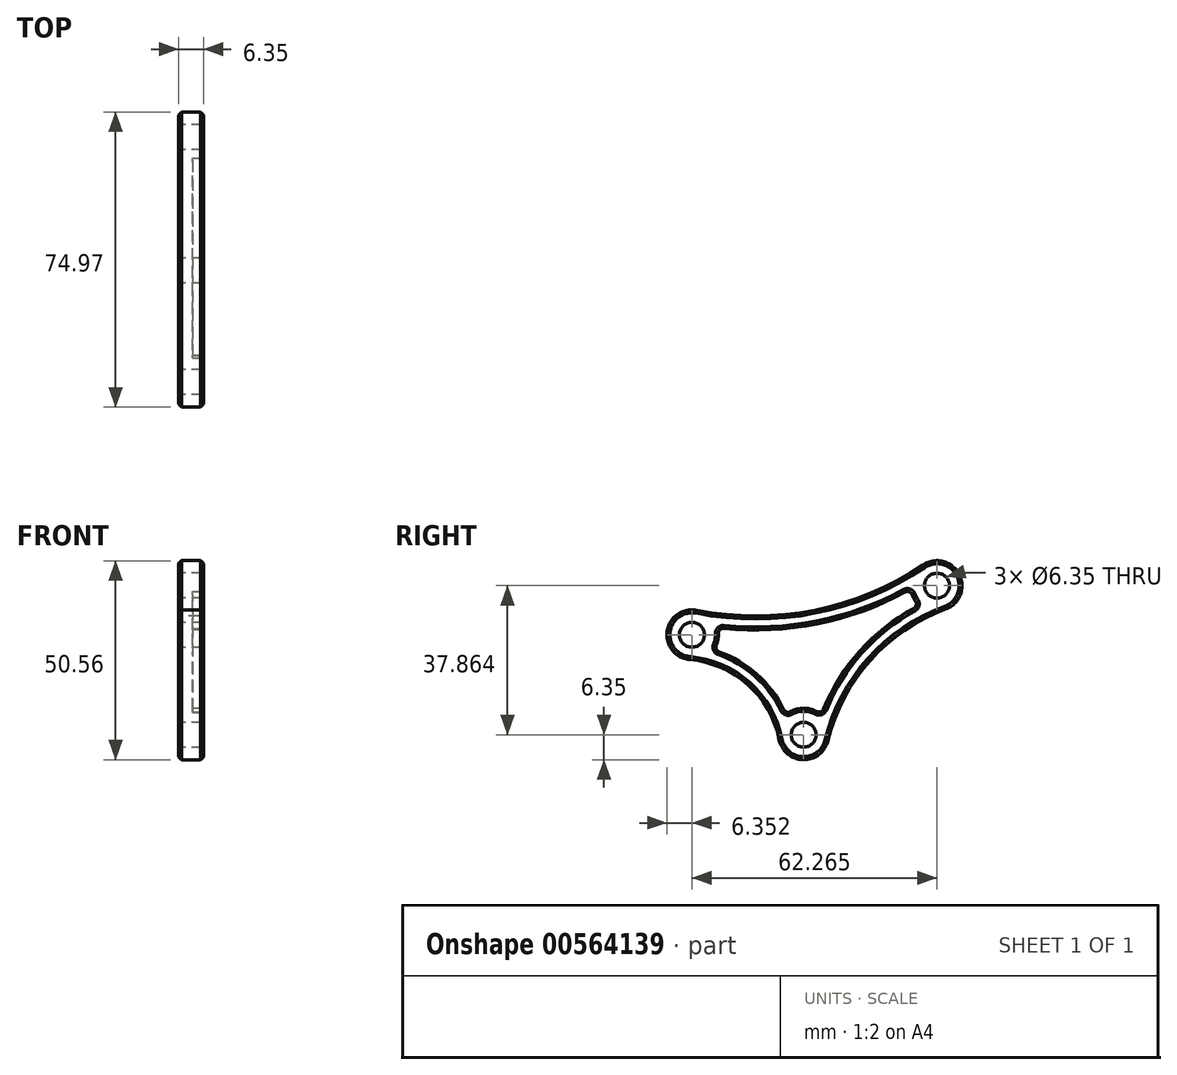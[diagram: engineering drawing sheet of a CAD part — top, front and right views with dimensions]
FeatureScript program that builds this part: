
annotation { "Feature Type Name" : "Feature", "Feature Type Description" : "" }
export const myFeature = defineFeature(function(context is Context, id is Id, definition is map)
    precondition{}
    {
        {
            var Q0;
            Q0=qCreatedBy(makeId("Right.planeOp"),FACE);
            var sketch = newSketch(context, id + "F0", { "sketchPlane" : qUnion([Q0])});
            skCircle(sketch, "E0", {"center": v(0, 0) * mm, "radius": 3.18 * mm});
            skCircle(sketch, "E1", {"center": v(33.87, 37.86) * mm, "radius": 3.18 * mm});
            skCircle(sketch, "E2", {"center": v(-28.4, 25.4) * mm, "radius": 3.18 * mm});
            skCircle(sketch, "E3", {"center": v(-28.4, 25.4) * mm, "radius": 6.35 * mm});
            skCircle(sketch, "E4", {"center": v(33.87, 37.86) * mm, "radius": 6.35 * mm});
            skCircle(sketch, "E5", {"center": v(0, 0) * mm, "radius": 6.35 * mm});
            skLineSegment(sketch, "E6", {"start": v(-28.4, 25.4) * mm, "end": v(33.87, 37.86) * mm});
            skLineSegment(sketch, "E7", {"start": v(0, 0) * mm, "end": v(-28.4, 25.4) * mm});
            skLineSegment(sketch, "E8", {"start": v(33.87, 37.86) * mm, "end": v(0, 0) * mm});
            skArc(sketch, "E9", {"start": v(-27.15, 31.63) * mm, "mid": v(2.73, 31.63) * mm, "end": v(30.32, 43.13) * mm});
            skArc(sketch, "E10", {"start": v(-6.23, -1.25) * mm, "mid": v(-14.2, 12.7) * mm, "end": v(-28.94, 19.07) * mm});
            skArc(sketch, "E11", {"start": v(36.05, 31.9) * mm, "mid": v(16.93, 18.93) * mm, "end": v(6.17, -1.5) * mm});
            skSolve(sketch);
        }
        {
            var Q0;
            {var subQ0=sQuery(id+"F0.wireOp",EDGE,"E9");var subQ1=sQuery(id+"F0.wireOp",EDGE,"E3");var subQ2=makeQuery(id+"F0.imprint","INTERSECT",VERTEX,{"derivedFrom":[subQ1,subQ0]});Q0=makeQuery(id+"F0.imprint","IMPRINT",FACE,{"disambiguationData":[TD([[makeQuery(id+"F0.imprint","IMPRINT",EDGE,{"disambiguationData":[TD([[subQ2,1.0]])],"derivedFrom":subQ1}),-1.0]])]});}
            var Q1;
            {var subQ0=sQuery(id+"F0.wireOp",EDGE,"E10");var subQ1=sQuery(id+"F0.wireOp",EDGE,"E3");var subQ2=makeQuery(id+"F0.imprint","INTERSECT",VERTEX,{"derivedFrom":[subQ1,subQ0]});Q1=makeQuery(id+"F0.imprint","IMPRINT",FACE,{"disambiguationData":[TD([[makeQuery(id+"F0.imprint","IMPRINT",EDGE,{"disambiguationData":[TD([[subQ2,-1.0]])],"derivedFrom":subQ1}),-1.0]])]});}
            var Q2;
            {var subQ0=sQuery(id+"F0.wireOp",EDGE,"E9");var subQ1=sQuery(id+"F0.wireOp",EDGE,"E4");var subQ2=makeQuery(id+"F0.imprint","INTERSECT",VERTEX,{"derivedFrom":[subQ1,subQ0]});Q2=makeQuery(id+"F0.imprint","IMPRINT",FACE,{"disambiguationData":[TD([[makeQuery(id+"F0.imprint","IMPRINT",EDGE,{"disambiguationData":[TD([[subQ2,-1.0]])],"derivedFrom":subQ1}),-1.0]])]});}
            var Q3;
            {var subQ0=sQuery(id+"F0.wireOp",EDGE,"E10");var subQ1=sQuery(id+"F0.wireOp",EDGE,"E5");var subQ2=makeQuery(id+"F0.imprint","INTERSECT",VERTEX,{"derivedFrom":[subQ1,subQ0]});Q3=makeQuery(id+"F0.imprint","IMPRINT",FACE,{"disambiguationData":[TD([[makeQuery(id+"F0.imprint","IMPRINT",EDGE,{"disambiguationData":[TD([[subQ2,1.0]])],"derivedFrom":subQ1}),-1.0]])]});}
            var Q4;
            {var subQ5=sQuery(id+"F0.wireOp",EDGE,"E7");var subQ6=sQuery(id+"F0.wireOp",EDGE,"E0");var subQ7=makeQuery(id+"F0.imprint","INTERSECT",VERTEX,{"derivedFrom":[subQ6,subQ5]});Q4=makeQuery(id+"F0.imprint","IMPRINT",FACE,{"disambiguationData":[TD([[makeQuery(id+"F0.imprint","IMPRINT",EDGE,{"disambiguationData":[TD([[subQ7,-1.0]])],"derivedFrom":subQ6}),-1.0]])]});}
            var Q5;
            {var subQ5=sQuery(id+"F0.wireOp",EDGE,"E6");var subQ7=sQuery(id+"F0.wireOp",EDGE,"E1");var subQ8=makeQuery(id+"F0.imprint","INTERSECT",VERTEX,{"derivedFrom":[subQ7,subQ5]});Q5=makeQuery(id+"F0.imprint","IMPRINT",FACE,{"disambiguationData":[TD([[makeQuery(id+"F0.imprint","IMPRINT",EDGE,{"disambiguationData":[TD([[subQ8,1.0]])],"derivedFrom":subQ7}),-1.0]])]});}
            var Q6;
            {var subQ4=sQuery(id+"F0.wireOp",EDGE,"E6");var subQ5=sQuery(id+"F0.wireOp",EDGE,"E2");var subQ6=makeQuery(id+"F0.imprint","INTERSECT",VERTEX,{"derivedFrom":[subQ5,subQ4]});Q6=makeQuery(id+"F0.imprint","IMPRINT",FACE,{"disambiguationData":[TD([[makeQuery(id+"F0.imprint","IMPRINT",EDGE,{"disambiguationData":[TD([[subQ6,-1.0]])],"derivedFrom":subQ5}),-1.0]])]});}
            var Q7;
            {var subQ0=sQuery(id+"F0.wireOp",EDGE,"E6");var subQ2=sQuery(id+"F0.wireOp",EDGE,"E3");var subQ3=makeQuery(id+"F0.imprint","INTERSECT",VERTEX,{"derivedFrom":[subQ2,subQ0]});Q7=makeQuery(id+"F0.imprint","IMPRINT",FACE,{"disambiguationData":[TD([[makeQuery(id+"F0.imprint","IMPRINT",EDGE,{"disambiguationData":[TD([[subQ3,1.0]])],"derivedFrom":subQ2}),-1.0]])]});}
            var Q8;
            {var subQ0=sQuery(id+"F0.wireOp",EDGE,"E6");var subQ1=sQuery(id+"F0.wireOp",EDGE,"E2");var subQ2=makeQuery(id+"F0.imprint","INTERSECT",VERTEX,{"derivedFrom":[subQ1,subQ0]});Q8=makeQuery(id+"F0.imprint","IMPRINT",FACE,{"disambiguationData":[TD([[makeQuery(id+"F0.imprint","IMPRINT",EDGE,{"disambiguationData":[TD([[subQ2,1.0]])],"derivedFrom":subQ1}),-1.0]])]});}
            var Q9;
            {var subQ0=sQuery(id+"F0.wireOp",EDGE,"E6");var subQ1=sQuery(id+"F0.wireOp",EDGE,"E1");var subQ2=makeQuery(id+"F0.imprint","INTERSECT",VERTEX,{"derivedFrom":[subQ1,subQ0]});Q9=makeQuery(id+"F0.imprint","IMPRINT",FACE,{"disambiguationData":[TD([[makeQuery(id+"F0.imprint","IMPRINT",EDGE,{"disambiguationData":[TD([[subQ2,-1.0]])],"derivedFrom":subQ1}),-1.0]])]});}
            var Q10;
            {var subQ0=sQuery(id+"F0.wireOp",EDGE,"E7");var subQ1=sQuery(id+"F0.wireOp",EDGE,"E0");var subQ2=makeQuery(id+"F0.imprint","INTERSECT",VERTEX,{"derivedFrom":[subQ1,subQ0]});Q10=makeQuery(id+"F0.imprint","IMPRINT",FACE,{"disambiguationData":[TD([[makeQuery(id+"F0.imprint","IMPRINT",EDGE,{"disambiguationData":[TD([[subQ2,1.0]])],"derivedFrom":subQ1}),-1.0]])]});}
            var Q11;
            {var subQ0=sQuery(id+"F0.wireOp",EDGE,"E11");var subQ1=sQuery(id+"F0.wireOp",EDGE,"E5");var subQ2=makeQuery(id+"F0.imprint","INTERSECT",VERTEX,{"derivedFrom":[subQ1,subQ0]});Q11=makeQuery(id+"F0.imprint","IMPRINT",FACE,{"disambiguationData":[TD([[makeQuery(id+"F0.imprint","IMPRINT",EDGE,{"disambiguationData":[TD([[subQ2,-1.0]])],"derivedFrom":subQ1}),-1.0]])]});}
            var Q12;
            {var subQ0=sQuery(id+"F0.wireOp",EDGE,"E11");var subQ1=sQuery(id+"F0.wireOp",EDGE,"E4");var subQ2=makeQuery(id+"F0.imprint","INTERSECT",VERTEX,{"derivedFrom":[subQ1,subQ0]});Q12=makeQuery(id+"F0.imprint","IMPRINT",FACE,{"disambiguationData":[TD([[makeQuery(id+"F0.imprint","IMPRINT",EDGE,{"disambiguationData":[TD([[subQ2,1.0]])],"derivedFrom":subQ1}),-1.0]])]});}
            var Q13;
            {var subQ7=sQuery(id+"F0.wireOp",EDGE,"s0z4VmjC-9Jtz-9oDN-pM9U-WHnKUmS6Y34w");Q13=makeQuery(id+"F0.imprint","IMPRINT",FACE,{"disambiguationData":[TD([[makeQuery(id+"F0.imprint","IMPRINT",EDGE,{"derivedFrom":subQ7}),-1.0]])]});}
            var Q14;
            {var subQ3=sQuery(id+"F0.wireOp",EDGE,"DwXPQsX5-wXzO-8GNt-yisA-XoadTiBy5RnP");Q14=makeQuery(id+"F0.imprint","IMPRINT",FACE,{"disambiguationData":[TD([[makeQuery(id+"F0.imprint","IMPRINT",EDGE,{"derivedFrom":subQ3}),1.0]])]});}
            extrude(context, id + "F1", {"entities" : qUnion([Q0, Q1, Q2, Q3, Q4, Q5, Q6, Q7, Q8, Q9, Q10, Q11, Q12, Q13, Q14]), "depth" : 6.35 * mm, "offsetDistance" : 25.4 * mm});
        }
        {
            var Q0;
            Q0=makeQuery(id+"F1.opExtrude","CAP_FACE",FACE,{"disambiguationData":[OSD([sQuery(id+"F0.wireOp",EDGE,"E0"),sQuery(id+"F0.wireOp",EDGE,"E1"),sQuery(id+"F0.wireOp",EDGE,"E2"),sQuery(id+"F0.wireOp",EDGE,"E3"),sQuery(id+"F0.wireOp",EDGE,"E4"),sQuery(id+"F0.wireOp",EDGE,"E5"),sQuery(id+"F0.wireOp",EDGE,"E9"),sQuery(id+"F0.wireOp",EDGE,"E10"),sQuery(id+"F0.wireOp",EDGE,"E11"),sQuery(id+"F0.wireOp",EDGE,"PK5ZVaKs-dKFb-WiuK-RSGF-PoLstMmSIUzS"),sQuery(id+"F0.wireOp",EDGE,"ZKiUtxdi-KNTW-w6NJ-hDFq-4Mbr4RkbHqFE"),sQuery(id+"F0.wireOp",EDGE,"eUfChSaK-SJPo-Qv41-HvOd-nlew1evdhoHB")])],"isStart":false});
            shell(context, id + "F2", {"entities" : qUnion([Q0]), "thickness" : 3.56 * mm});
        }
        {
            var Q0;
            Q0=makeQuery(id+"F2.opShell","TWEAK_EDGE",EDGE,{"derivedFrom":[makeQuery(id+"F1.opExtrude","SWEPT_FACE",FACE,{"disambiguationData":[OSD([sQuery(id+"F0.wireOp",EDGE,"E2")])]}),makeQuery(id+"F1.opExtrude","SWEPT_FACE",FACE,{"disambiguationData":[OSD([sQuery(id+"F0.wireOp",EDGE,"E9")])]})]});
            var Q1;
            Q1=makeQuery(id+"F2.opShell","TWEAK_EDGE",EDGE,{"derivedFrom":[makeQuery(id+"F1.opExtrude","SWEPT_FACE",FACE,{"disambiguationData":[OSD([sQuery(id+"F0.wireOp",EDGE,"E2")])]}),makeQuery(id+"F1.opExtrude","SWEPT_FACE",FACE,{"disambiguationData":[OSD([sQuery(id+"F0.wireOp",EDGE,"E10")])]})]});
            var Q2;
            Q2=makeQuery(id+"F2.opShell","TWEAK_EDGE",EDGE,{"derivedFrom":[makeQuery(id+"F1.opExtrude","SWEPT_FACE",FACE,{"disambiguationData":[OSD([sQuery(id+"F0.wireOp",EDGE,"E0")])]}),makeQuery(id+"F1.opExtrude","SWEPT_FACE",FACE,{"disambiguationData":[OSD([sQuery(id+"F0.wireOp",EDGE,"E10")])]})]});
            var Q3;
            Q3=makeQuery(id+"F2.opShell","TWEAK_EDGE",EDGE,{"derivedFrom":[makeQuery(id+"F1.opExtrude","SWEPT_FACE",FACE,{"disambiguationData":[OSD([sQuery(id+"F0.wireOp",EDGE,"E0")])]}),makeQuery(id+"F1.opExtrude","SWEPT_FACE",FACE,{"disambiguationData":[OSD([sQuery(id+"F0.wireOp",EDGE,"E11")])]})]});
            var Q4;
            Q4=makeQuery(id+"F2.opShell","TWEAK_EDGE",EDGE,{"derivedFrom":[makeQuery(id+"F1.opExtrude","SWEPT_FACE",FACE,{"disambiguationData":[OSD([sQuery(id+"F0.wireOp",EDGE,"E1")])]}),makeQuery(id+"F1.opExtrude","SWEPT_FACE",FACE,{"disambiguationData":[OSD([sQuery(id+"F0.wireOp",EDGE,"E9")])]})]});
            var Q5;
            Q5=makeQuery(id+"F2.opShell","TWEAK_EDGE",EDGE,{"derivedFrom":[makeQuery(id+"F1.opExtrude","SWEPT_FACE",FACE,{"disambiguationData":[OSD([sQuery(id+"F0.wireOp",EDGE,"E1")])]}),makeQuery(id+"F1.opExtrude","SWEPT_FACE",FACE,{"disambiguationData":[OSD([sQuery(id+"F0.wireOp",EDGE,"E11")])]})]});
            fillet(context, id + "F3", {"entities" : qUnion([Q0, Q1, Q2, Q3, Q4, Q5]), "radius" : 1.27 * mm, "tangentPropagation" : true, "allowEdgeOverflow" : false});
        }
        {
            var Q0;
            Q0=makeQuery(id+"F1.opExtrude","CAP_EDGE",EDGE,{"disambiguationData":[OSD([sQuery(id+"F0.wireOp",EDGE,"E9")])],"isStart":false});
            var Q1;
            {var subQ0=sQuery(id+"F0.wireOp",EDGE,"E10");Q1=makeQuery(id+"F2.opShell","OFFSET_EDGE",EDGE,{"disambiguationData":[OSD([subQ0]),TDD([makeQuery(id+"F1.opExtrude","CAP_EDGE",EDGE,{"disambiguationData":[OSD([subQ0])],"isStart":false})])]});}
            var Q2;
            Q2=makeQuery(id+"F1.opExtrude","CAP_EDGE",EDGE,{"disambiguationData":[OSD([sQuery(id+"F0.wireOp",EDGE,"E9")])],"isStart":true});
            chamfer(context, id + "F4", {"entities" : qUnion([Q0, Q1, Q2]), "width" : 0.76 * mm, "tangentPropagation" : true});
        }
    });
